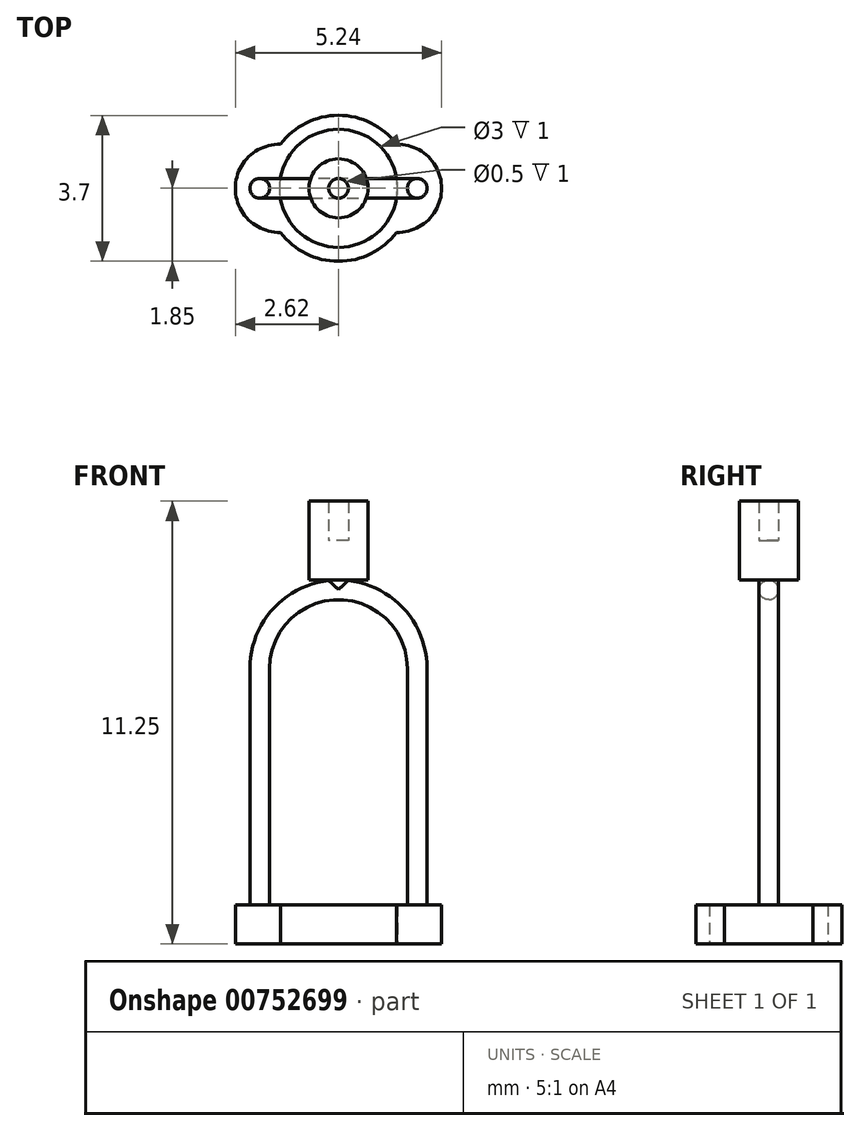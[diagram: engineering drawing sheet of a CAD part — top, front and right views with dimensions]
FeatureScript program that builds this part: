
annotation { "Feature Type Name" : "Feature", "Feature Type Description" : "" }
export const myFeature = defineFeature(function(context is Context, id is Id, definition is map)
    precondition{}
    {
        {
            var Q0;
            Q0=qCreatedBy(makeId("Top.planeOp"),FACE);
            var sketch = newSketch(context, id + "F0", { "sketchPlane" : qUnion([Q0])});
            skCircle(sketch, "E0", {"center": v(0, 0) * mm, "radius": 1.5 * mm});
            skCircle(sketch, "E1", {"center": v(0, 0) * mm, "radius": 3 * mm});
            skLineSegment(sketch, "E2", {"start": v(-1.5, 0) * mm, "end": v(-1.85, 0) * mm});
            skCircle(sketch, "E3", {"center": v(-1.5, 0) * mm, "radius": 1.12 * mm});
            skCircle(sketch, "E4", {"center": v(0, 0) * mm, "radius": 1.85 * mm});
            skCircle(sketch, "E5", {"center": v(1.5, 0) * mm, "radius": 1.12 * mm});
            skSolve(sketch);
        }
        {
            var Q0;
            {var subQ0=sQuery(id+"F0.wireOp",EDGE,"E2");Q0=makeQuery(id+"F0.imprint","IMPRINT",FACE,{"disambiguationData":[TD([[makeQuery(id+"F0.imprint","IMPRINT",EDGE,{"derivedFrom":subQ0}),-1.0]])]});}
            var Q1;
            {var subQ0=sQuery(id+"F0.wireOp",EDGE,"E4");var subQ1=sQuery(id+"F0.wireOp",EDGE,"E3");var subQ2=makeQuery(id+"F0.imprint","INTERSECT",VERTEX,{"disambiguationData":[OD(0.0)],"derivedFrom":[subQ1,subQ0]});Q1=makeQuery(id+"F0.imprint","IMPRINT",FACE,{"disambiguationData":[TD([[makeQuery(id+"F0.imprint","IMPRINT",EDGE,{"disambiguationData":[TD([[subQ2,-1.0]])],"derivedFrom":subQ1}),1.0]])]});}
            var Q2;
            {var subQ0=sQuery(id+"F0.wireOp",EDGE,"E2");Q2=makeQuery(id+"F0.imprint","IMPRINT",FACE,{"disambiguationData":[TD([[makeQuery(id+"F0.imprint","IMPRINT",EDGE,{"derivedFrom":subQ0}),1.0]])]});}
            var Q3;
            {var subQ0=sQuery(id+"F0.wireOp",EDGE,"E3");var subQ1=sQuery(id+"F0.wireOp",EDGE,"E0");var subQ2=makeQuery(id+"F0.imprint","INTERSECT",VERTEX,{"disambiguationData":[OD(1.0)],"derivedFrom":[subQ1,subQ0]});Q3=makeQuery(id+"F0.imprint","IMPRINT",FACE,{"disambiguationData":[TD([[makeQuery(id+"F0.imprint","IMPRINT",EDGE,{"disambiguationData":[TD([[subQ2,-1.0]])],"derivedFrom":subQ1}),-1.0]])]});}
            var Q4;
            {var subQ0=sQuery(id+"F0.wireOp",EDGE,"E3");var subQ1=sQuery(id+"F0.wireOp",EDGE,"E0");var subQ2=makeQuery(id+"F0.imprint","INTERSECT",VERTEX,{"disambiguationData":[OD(0.0)],"derivedFrom":[subQ1,subQ0]});Q4=makeQuery(id+"F0.imprint","IMPRINT",FACE,{"disambiguationData":[TD([[makeQuery(id+"F0.imprint","IMPRINT",EDGE,{"disambiguationData":[TD([[subQ2,1.0]])],"derivedFrom":subQ1}),-1.0]])]});}
            var Q5;
            {var subQ0=sQuery(id+"F0.wireOp",EDGE,"E5");var subQ1=sQuery(id+"F0.wireOp",EDGE,"E4");var subQ2=makeQuery(id+"F0.imprint","INTERSECT",VERTEX,{"disambiguationData":[OD(0.0)],"derivedFrom":[subQ1,subQ0]});Q5=makeQuery(id+"F0.imprint","IMPRINT",FACE,{"disambiguationData":[TD([[makeQuery(id+"F0.imprint","IMPRINT",EDGE,{"disambiguationData":[TD([[subQ2,1.0]])],"derivedFrom":subQ1}),-1.0]])]});}
            var Q6;
            {var subQ0=sQuery(id+"F0.wireOp",EDGE,"E5");var subQ1=sQuery(id+"F0.wireOp",EDGE,"E0");var subQ2=makeQuery(id+"F0.imprint","INTERSECT",VERTEX,{"disambiguationData":[OD(0.0)],"derivedFrom":[subQ1,subQ0]});Q6=makeQuery(id+"F0.imprint","IMPRINT",FACE,{"disambiguationData":[TD([[makeQuery(id+"F0.imprint","IMPRINT",EDGE,{"disambiguationData":[TD([[subQ2,1.0]])],"derivedFrom":subQ1}),-1.0]])]});}
            extrude(context, id + "F1", {"entities" : qUnion([Q0, Q1, Q2, Q3, Q4, Q5, Q6]), "depth" : 1 * mm, "offsetDistance" : 25 * mm});
        }
        {
            var Q0;
            Q0=qCreatedBy(makeId("Front.planeOp"),FACE);
            var sketch = newSketch(context, id + "F2", { "sketchPlane" : qUnion([Q0])});
            skLineSegment(sketch, "E6", {"start": v(-2, 0) * mm, "end": v(-2, 7) * mm});
            skLineSegment(sketch, "E7", {"start": v(-2, 0) * mm, "end": v(0, 0) * mm});
            skLineSegment(sketch, "E8", {"start": v(2, 0) * mm, "end": v(2, 7) * mm});
            skArc(sketch, "E9", {"start": v(2, 7) * mm, "mid": v(0, 9) * mm, "end": v(-2, 7) * mm});
            skLineSegment(sketch, "E10", {"start": v(0, 9) * mm, "end": v(2, 9) * mm});
            skSolve(sketch);
        }
        {
            var Q0;
            Q0=makeQuery(id+"F1.opExtrude","CAP_FACE",FACE,{"disambiguationData":[OSD([sQuery(id+"F0.wireOp",EDGE,"E0"),sQuery(id+"F0.wireOp",EDGE,"E3"),sQuery(id+"F0.wireOp",EDGE,"E4"),sQuery(id+"F0.wireOp",EDGE,"E5")])],"isStart":true});
            var sketch = newSketch(context, id + "F3", { "sketchPlane" : qUnion([Q0])});
            skCircle(sketch, "E11", {"center": v(2, 0) * mm, "radius": 0.25 * mm});
            skSolve(sketch);
        }
        {
            var Q0;
            Q0=makeQuery(id+"F3.imprint","IMPRINT",FACE,{"disambiguationData":[TD([[makeQuery(id+"F3.imprint","IMPRINT",EDGE,{"derivedFrom":sQuery(id+"F3.wireOp",EDGE,"E11")}),1.0]])]});
            var Q1;
            Q1=sQuery(id+"F2.wireOp",EDGE,"E8");
            var Q2;
            Q2=sQuery(id+"F2.wireOp",EDGE,"E9");
            var Q3;
            Q3=sQuery(id+"F2.wireOp",EDGE,"E6");
            sweep(context, id + "F4", {"operationType" : NewBodyOperationType.ADD, "profiles" : qUnion([Q0]), "path" : qUnion([Q1, Q2, Q3])});
        }
        {
            var Q0;
            Q0=qCreatedBy(makeId("Top.planeOp"),FACE);
            cPlane(context, id + "F5", {"entities" : qUnion([Q0]), "cplaneType" : CPlaneType.OFFSET, "offset" : 9.25 * mm, "width" : 150 * mm, "height" : 150 * mm});
        }
        {
            var Q0;
            Q0=qCreatedBy(id+"F5.planeOp",FACE);
            var sketch = newSketch(context, id + "F6", { "sketchPlane" : qUnion([Q0])});
            skCircle(sketch, "E12", {"center": v(0, 0) * mm, "radius": 0.25 * mm});
            skCircle(sketch, "E13", {"center": v(0, 0) * mm, "radius": 0.75 * mm});
            skSolve(sketch);
        }
        {
            var Q0;
            Q0=makeQuery(id+"F6.imprint","IMPRINT",FACE,{"disambiguationData":[TD([[makeQuery(id+"F6.imprint","IMPRINT",EDGE,{"derivedFrom":sQuery(id+"F6.wireOp",EDGE,"E12")}),1.0]])]});
            extrude(context, id + "F7", {"entities" : qUnion([Q0]), "operationType" : NewBodyOperationType.ADD, "depth" : 1 * mm, "offsetDistance" : 25 * mm, "hasSecondDirection" : true, "secondDirectionOppositeDirection" : true, "secondDirectionDepth" : .25 * mm});
        }
        {
            var Q0;
            Q0=makeQuery(id+"F6.imprint","IMPRINT",FACE,{"disambiguationData":[TD([[makeQuery(id+"F6.imprint","IMPRINT",EDGE,{"derivedFrom":sQuery(id+"F6.wireOp",EDGE,"E12")}),-1.0]])]});
            extrude(context, id + "F8", {"entities" : qUnion([Q0]), "operationType" : NewBodyOperationType.ADD, "depth" : 2 * mm, "offsetDistance" : 25 * mm});
        }
    });
